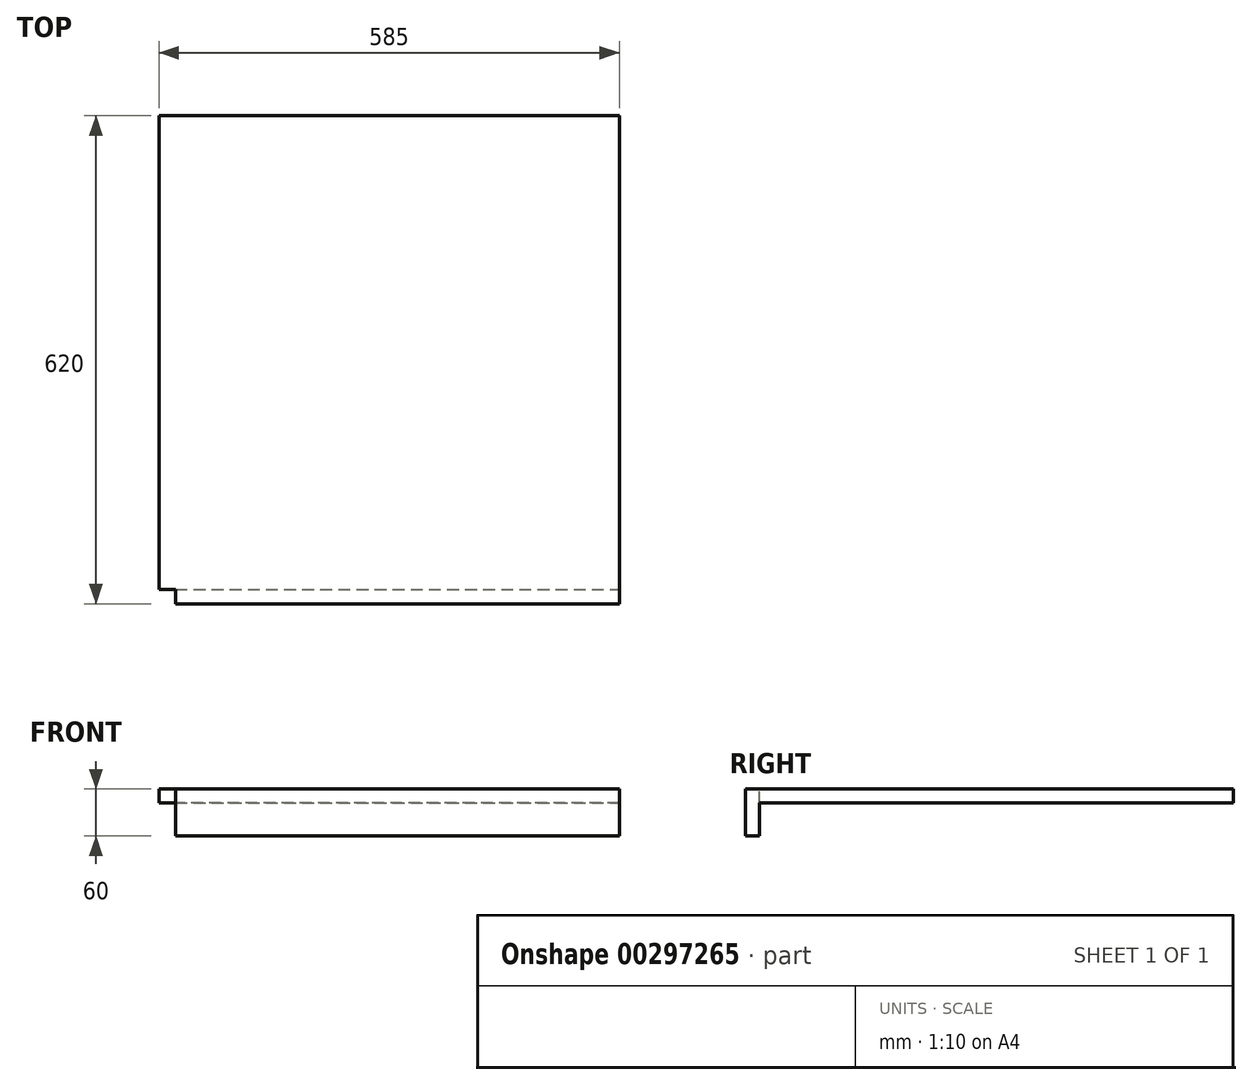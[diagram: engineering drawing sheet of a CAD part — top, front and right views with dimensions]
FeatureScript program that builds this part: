
annotation { "Feature Type Name" : "Feature", "Feature Type Description" : "" }
export const myFeature = defineFeature(function(context is Context, id is Id, definition is map)
    precondition{}
    {
        {
            var Q0;
            Q0=qCreatedBy(makeId("Top.planeOp"),FACE);
            var sketch = newSketch(context, id + "F0", { "sketchPlane" : qUnion([Q0])});
            skLineSegment(sketch, "E0.bottom", {"start": v(292.5, -310) * mm, "end": v(-292.5, -310) * mm});
            skLineSegment(sketch, "E0.top", {"start": v(292.5, 310) * mm, "end": v(-292.5, 310) * mm});
            skLineSegment(sketch, "E0.left", {"start": v(292.5, -310) * mm, "end": v(292.5, 310) * mm});
            skLineSegment(sketch, "E0.right", {"start": v(-292.5, -310) * mm, "end": v(-292.5, 310) * mm});
            skPoint(sketch, "E0.middle", {"position": v(0, 0) * mm});
            skSolve(sketch);
        }
        {
            var Q0;
            Q0=qSketchRegion(id+"F0",true);
            extrude(context, id + "F1", {"entities" : qUnion([Q0]), "depth" : 18 * mm});
        }
        {
            var Q0;
            Q0=makeQuery(id+"F1.opExtrude","CAP_FACE",FACE,{"disambiguationData":[OSD([sQuery(id+"F0.wireOp",EDGE,"E0.bottom"),sQuery(id+"F0.wireOp",EDGE,"E0.top"),sQuery(id+"F0.wireOp",EDGE,"E0.left"),sQuery(id+"F0.wireOp",EDGE,"E0.right")])],"isStart":true});
            var sketch = newSketch(context, id + "F2", { "sketchPlane" : qUnion([Q0])});
            skLineSegment(sketch, "E1.bottom", {"start": v(-292.5, 310) * mm, "end": v(292.5, 310) * mm});
            skLineSegment(sketch, "E1.top", {"start": v(-292.5, 292) * mm, "end": v(292.5, 292) * mm});
            skLineSegment(sketch, "E1.left", {"start": v(-292.5, 310) * mm, "end": v(-292.5, 292) * mm});
            skLineSegment(sketch, "E1.right", {"start": v(292.5, 310) * mm, "end": v(292.5, 292) * mm});
            skSolve(sketch);
        }
        {
            var Q0;
            Q0=qSketchRegion(id+"F2",true);
            extrude(context, id + "F3", {"entities" : qUnion([Q0]), "operationType" : NewBodyOperationType.ADD, "depth" : 42 * mm});
        }
        {
            var Q0;
            Q0=makeQuery(id+"F1.opExtrude","CAP_FACE",FACE,{"disambiguationData":[OSD([sQuery(id+"F0.wireOp",EDGE,"E0.bottom"),sQuery(id+"F0.wireOp",EDGE,"E0.top"),sQuery(id+"F0.wireOp",EDGE,"E0.left"),sQuery(id+"F0.wireOp",EDGE,"E0.right")])],"isStart":false});
            var sketch = newSketch(context, id + "F4", { "sketchPlane" : qUnion([Q0])});
            skLineSegment(sketch, "E2.bottom", {"start": v(-292.5, -310) * mm, "end": v(-271.5, -310) * mm});
            skLineSegment(sketch, "E2.top", {"start": v(-292.5, -292) * mm, "end": v(-271.5, -292) * mm});
            skLineSegment(sketch, "E2.left", {"start": v(-292.5, -310) * mm, "end": v(-292.5, -292) * mm});
            skLineSegment(sketch, "E2.right", {"start": v(-271.5, -310) * mm, "end": v(-271.5, -292) * mm});
            skSolve(sketch);
        }
        {
            var Q0;
            Q0=qSketchRegion(id+"F4",true);
            extrude(context, id + "F5", {"entities" : qUnion([Q0]), "operationType" : NewBodyOperationType.REMOVE, "oppositeDirection" : true, "depth" : 60 * mm});
        }
    });
